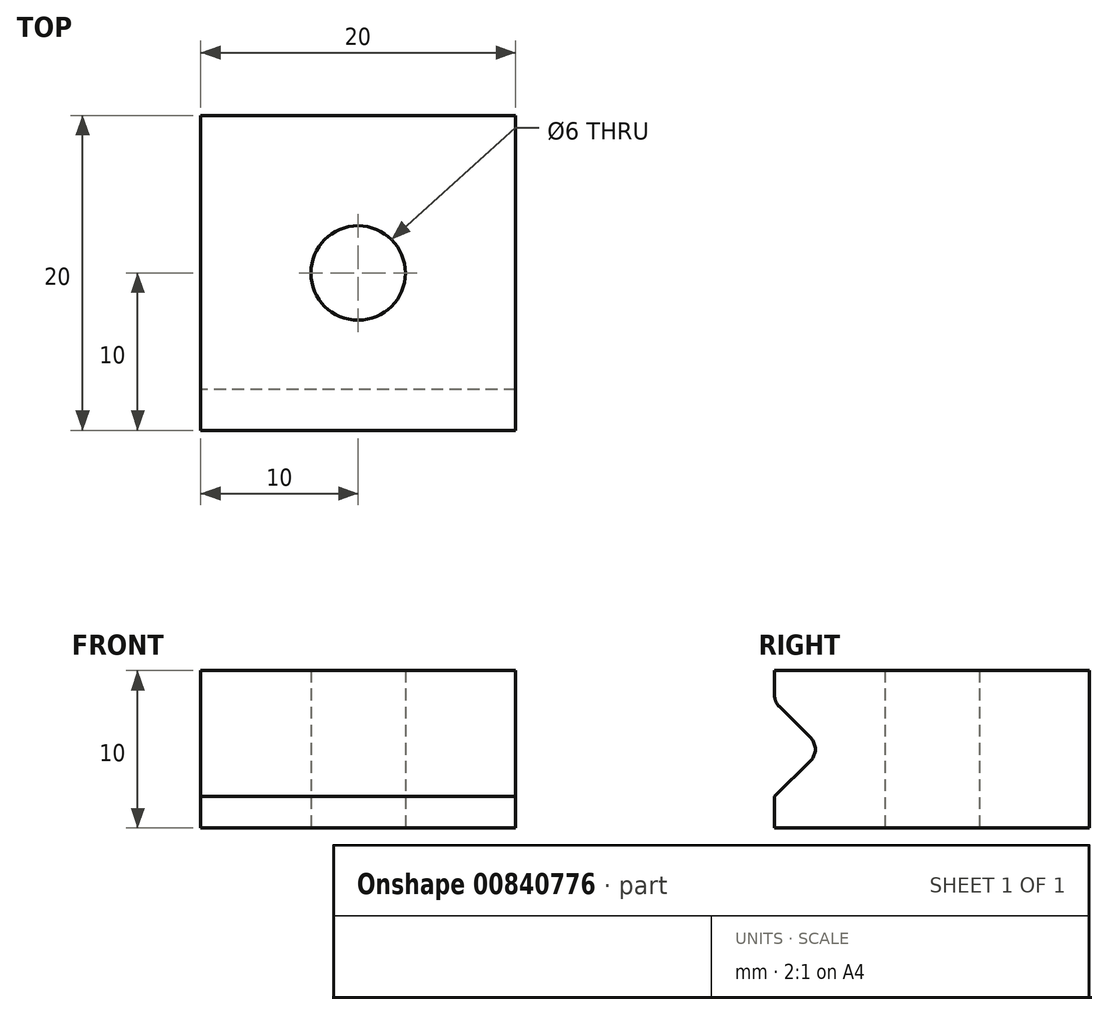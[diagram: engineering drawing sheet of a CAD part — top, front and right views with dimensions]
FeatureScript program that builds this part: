
annotation { "Feature Type Name" : "Feature", "Feature Type Description" : "" }
export const myFeature = defineFeature(function(context is Context, id is Id, definition is map)
    precondition{}
    {
        {
            var Q0;
            Q0=qCreatedBy(makeId("Top.planeOp"),FACE);
            var sketch = newSketch(context, id + "F0", { "sketchPlane" : qUnion([Q0])});
            skLineSegment(sketch, "E0.bottom", {"start": v(10, -10) * mm, "end": v(-10, -10) * mm});
            skLineSegment(sketch, "E0.top", {"start": v(10, 10) * mm, "end": v(-10, 10) * mm});
            skLineSegment(sketch, "E0.left", {"start": v(10, -10) * mm, "end": v(10, 10) * mm});
            skLineSegment(sketch, "E0.right", {"start": v(-10, -10) * mm, "end": v(-10, 10) * mm});
            skPoint(sketch, "E0.middle", {"position": v(0, 0) * mm});
            skCircle(sketch, "E1", {"center": v(0, 0) * mm, "radius": 3 * mm});
            skSolve(sketch);
        }
        {
            var Q0;
            Q0=makeQuery(id+"F0.imprint","IMPRINT",FACE,{"disambiguationData":[TD([[makeQuery(id+"F0.imprint","IMPRINT",EDGE,{"derivedFrom":sQuery(id+"F0.wireOp",EDGE,"E0.bottom")}),-1.0]])]});
            extrude(context, id + "F1", {"entities" : qUnion([Q0]), "depth" : 10 * mm, "offsetDistance" : 25 * mm});
        }
        {
            var Q0;
            Q0=makeQuery(id+"F1.opExtrude","SWEPT_FACE",FACE,{"disambiguationData":[OSD([sQuery(id+"F0.wireOp",EDGE,"E0.left")])]});
            var sketch = newSketch(context, id + "F2", { "sketchPlane" : qUnion([Q0])});
            skLineSegment(sketch, "E2", {"start": v(-10, 8) * mm, "end": v(-7, 5) * mm});
            skLineSegment(sketch, "E3", {"start": v(-7, 5) * mm, "end": v(-10, 2) * mm});
            skSolve(sketch);
        }
        {
            var Q0;
            {var subQ0=sQuery(id+"F2.wireOp",EDGE,"E2");Q0=makeQuery(id+"F2.imprint","IMPRINT",FACE,{"disambiguationData":[TD([[makeQuery(id+"F2.imprint","IMPRINT",EDGE,{"derivedFrom":subQ0}),-1.0]])]});}
            extrude(context, id + "F3", {"entities" : qUnion([Q0]), "operationType" : NewBodyOperationType.REMOVE, "endBound" : BoundingType.UP_TO_NEXT, "oppositeDirection" : true, "depth" : 25 * mm, "offsetDistance" : 25 * mm});
        }
        {
            var Q0;
            Q0=makeQuery(id+"F3.boolean.opBoolean","COPY",EDGE,{"derivedFrom":makeQuery(id+"F3.opExtrude","SWEPT_EDGE",EDGE,{"disambiguationData":[OSD([sQuery(id+"F2.wireOp",EDGE,"E2"),sQuery(id+"F2.wireOp",EDGE,"E3")])]})});
            var Q1;
            Q1=makeQuery(id+"F3.boolean.opBoolean","COPY",EDGE,{"derivedFrom":makeQuery(id+"F3.opExtrude","SWEPT_EDGE",EDGE,{"disambiguationData":[OSD([sQuery(id+"F0.wireOp",EDGE,"E0.bottom"),sQuery(id+"F0.wireOp",EDGE,"E0.left"),sQuery(id+"F2.wireOp",EDGE,"E2")])]})});
            var Q2;
            Q2=makeQuery(id+"F3.boolean.opBoolean","COPY",EDGE,{"derivedFrom":makeQuery(id+"F3.opExtrude","SWEPT_EDGE",EDGE,{"disambiguationData":[OSD([sQuery(id+"F0.wireOp",EDGE,"E0.bottom"),sQuery(id+"F0.wireOp",EDGE,"E0.left"),sQuery(id+"F2.wireOp",EDGE,"E3")])]})});
            fillet(context, id + "F4", {"entities" : qUnion([Q0, Q1, Q2]), "radius" : 1 * mm, "tangentPropagation" : true, "allowEdgeOverflow" : false});
        }
    });
